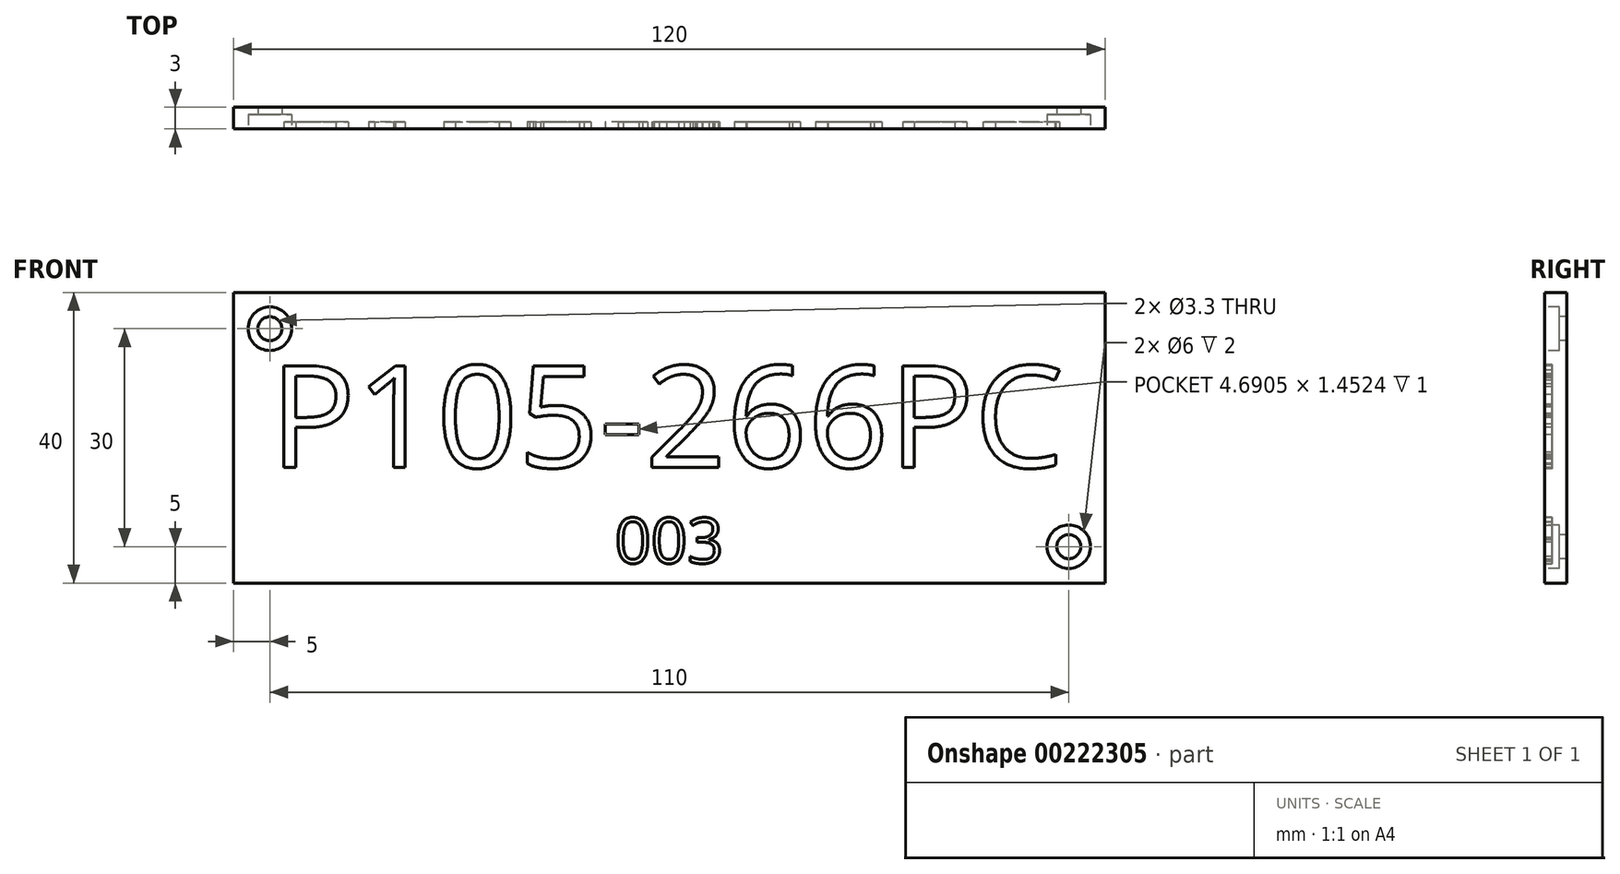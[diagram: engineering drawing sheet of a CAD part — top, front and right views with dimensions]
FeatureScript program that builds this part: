
annotation { "Feature Type Name" : "Feature", "Feature Type Description" : "" }
export const myFeature = defineFeature(function(context is Context, id is Id, definition is map)
    precondition{}
    {
        {
            var Q0;
            Q0=qCreatedBy(makeId("Front.planeOp"),FACE);
            var sketch = newSketch(context, id + "F0", { "sketchPlane" : qUnion([Q0])});
            skLineSegment(sketch, "E0.bottom", {"start": v(60, -20) * mm, "end": v(-60, -20) * mm});
            skLineSegment(sketch, "E0.top", {"start": v(60, 20) * mm, "end": v(-60, 20) * mm});
            skLineSegment(sketch, "E0.left", {"start": v(60, -20) * mm, "end": v(60, 20) * mm});
            skLineSegment(sketch, "E0.right", {"start": v(-60, -20) * mm, "end": v(-60, 20) * mm});
            skPoint(sketch, "E0.middle", {"position": v(0, 0) * mm});
            skSolve(sketch);
        }
        {
            var Q0;
            Q0=makeQuery(id+"F0.imprint","IMPRINT",FACE,{"disambiguationData":[TD([[makeQuery(id+"F0.imprint","IMPRINT",EDGE,{"derivedFrom":sQuery(id+"F0.wireOp",EDGE,"E0.bottom")}),-1.0]])]});
            extrude(context, id + "F1", {"entities" : qUnion([Q0]), "depth" : 3 * mm});
        }
        {
            var Q0;
            Q0=makeQuery(id+"F1.opExtrude","CAP_FACE",FACE,{"disambiguationData":[OSD([sQuery(id+"F0.wireOp",EDGE,"E0.bottom"),sQuery(id+"F0.wireOp",EDGE,"E0.top"),sQuery(id+"F0.wireOp",EDGE,"E0.left"),sQuery(id+"F0.wireOp",EDGE,"E0.right")])],"isStart":false});
            var sketch = newSketch(context, id + "F2", { "sketchPlane" : qUnion([Q0])});
            skPoint(sketch, "E1", {"position": v(-55, 15) * mm});
            skPoint(sketch, "E2", {"position": v(55, -15) * mm});
            skSolve(sketch);
        }
        {
            var Q0;
            Q0=sQuery(id+"F2.wireOp",VERTEX,"E1");
            var Q1;
            Q1=sQuery(id+"F2.wireOp",VERTEX,"E2");
            var Q2;
            Q2=makeQuery(id+"F1.opExtrude","SWEPT_BODY",BODY,{"disambiguationData":[OSD([sQuery(id+"F0.wireOp",EDGE,"E0.bottom"),sQuery(id+"F0.wireOp",EDGE,"E0.top"),sQuery(id+"F0.wireOp",EDGE,"E0.left"),sQuery(id+"F0.wireOp",EDGE,"E0.right")])]});
            hole(context, id + "F3", {"style" : HoleStyle.C_BORE, "endStyle" : HoleEndStyle.THROUGH, "holeDiameter" : 3.3 * mm, "cBoreDiameter" : 6 * mm, "cBoreDepth" : 2 * mm, "locations" : qUnion([Q0, Q1]), "scope" : qUnion([Q2]), "isTappedThrough" : true});
        }
        {
            var Q0;
            Q0=makeQuery(id+"F1.opExtrude","CAP_FACE",FACE,{"disambiguationData":[OSD([sQuery(id+"F0.wireOp",EDGE,"E0.bottom"),sQuery(id+"F0.wireOp",EDGE,"E0.top"),sQuery(id+"F0.wireOp",EDGE,"E0.left"),sQuery(id+"F0.wireOp",EDGE,"E0.right")])],"isStart":false});
            var sketch = newSketch(context, id + "F4", { "sketchPlane" : qUnion([Q0])});
            skText(sketch, "E3", { "text": "P105-266PC", "fontName": "OpenSans-Regular.ttf"});
            const initialGuessF4  = {"E3": [-0.055, -0.00409, 1, 0, 0.01409]};
            skSetInitialGuess(sketch, initialGuessF4);
            skSolve(sketch);
        }
        {
            var Q0;
            Q0 = qSketchRegion(id + "F4", true);
            extrude(context, id + "F5", {"entities" : qUnion([Q0]), "operationType" : NewBodyOperationType.REMOVE, "oppositeDirection" : true, "depth" : 1 * mm});
        }
        {
            var Q0;
            {var subQ0=sQuery(id+"F0.wireOp",EDGE,"E0.right");var subQ1=sQuery(id+"F0.wireOp",EDGE,"E0.left");var subQ2=sQuery(id+"F0.wireOp",EDGE,"E0.top");var subQ3=sQuery(id+"F0.wireOp",EDGE,"E0.bottom");Q0=makeQuery(id+"F5.boolean.opBoolean","SPLIT",FACE,{"disambiguationData":[TD([makeQuery(id+"F1.opExtrude","SWEPT_FACE",FACE,{"disambiguationData":[OSD([subQ3])]})])],"derivedFrom":makeQuery(id+"F1.opExtrude","CAP_FACE",FACE,{"disambiguationData":[OSD([subQ3,subQ2,subQ1,subQ0])],"isStart":false})});}
            var sketch = newSketch(context, id + "F6", { "sketchPlane" : qUnion([Q0])});
            skText(sketch, "E4", { "text": "003", "fontName": "OpenSans-Regular.ttf"});
            const initialGuessF6  = {"E4": [-0.0075, -0.01727, 1, 0, 0.00627]};
            skSetInitialGuess(sketch, initialGuessF6);
            skSolve(sketch);
        }
        {
            var Q0;
            Q0 = qSketchRegion(id + "F6", true);
            extrude(context, id + "F7", {"entities" : qUnion([Q0]), "operationType" : NewBodyOperationType.REMOVE, "oppositeDirection" : true, "depth" : 1 * mm});
        }
    });
